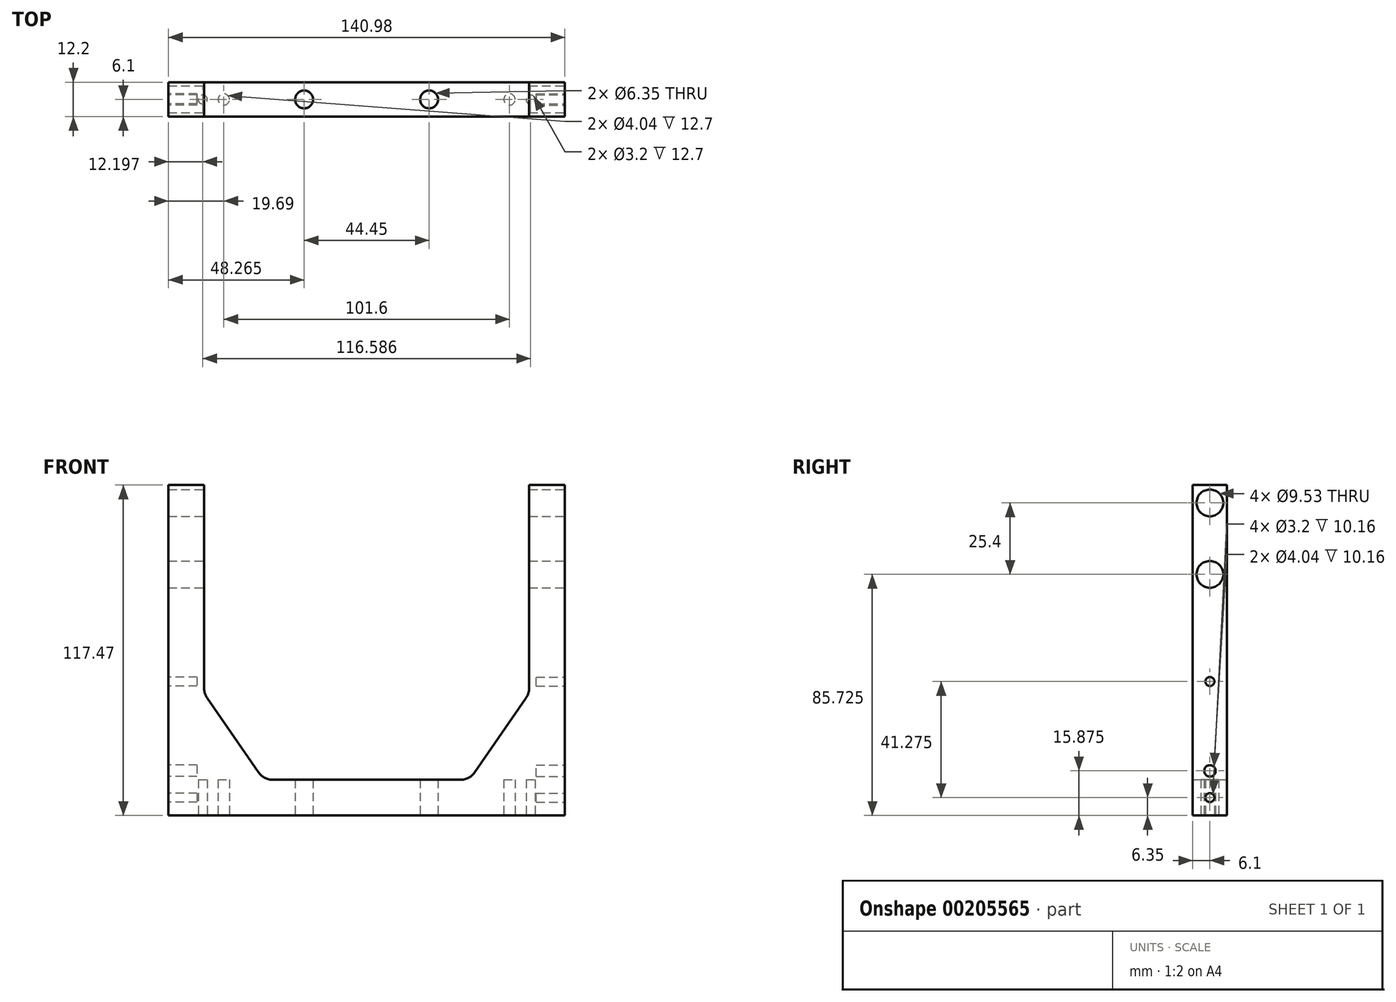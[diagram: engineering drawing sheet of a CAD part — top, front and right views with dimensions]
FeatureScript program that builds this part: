
annotation { "Feature Type Name" : "Feature", "Feature Type Description" : "" }
export const myFeature = defineFeature(function(context is Context, id is Id, definition is map)
    precondition{}
    {
        {
            var Q0;
            Q0=qCreatedBy(makeId("Front.planeOp"),FACE);
            var sketch = newSketch(context, id + "F0", { "sketchPlane" : qUnion([Q0])});
            skLineSegment(sketch, "E0", {"start": v(0, 0) * mm, "end": v(70.48, 0) * mm});
            skLineSegment(sketch, "E1", {"start": v(70.48, 0) * mm, "end": v(70.48, 117.48) * mm});
            skLineSegment(sketch, "E2", {"start": v(70.48, 117.48) * mm, "end": v(57.78, 117.48) * mm});
            skLineSegment(sketch, "E3", {"start": v(57.79, 117.48) * mm, "end": v(57.79, 45.31) * mm});
            skLineSegment(sketch, "E4", {"start": v(33.27, 12.7) * mm, "end": v(0, 12.7) * mm});
            skArc(sketch, "E5", {"start": v(56.66, 41.7) * mm, "mid": v(57.5, 43.42) * mm, "end": v(57.79, 45.31) * mm});
            skArc(sketch, "E6", {"start": v(33.27, 12.7) * mm, "mid": v(36.22, 13.43) * mm, "end": v(38.5, 15.44) * mm});
            skLineSegment(sketch, "E7", {"start": v(38.5, 15.44) * mm, "end": v(56.66, 41.7) * mm});
            skArc(sketch, "E8.MirrorCS", {"start": v(-33.27, 12.7) * mm, "mid": v(-36.22, 13.43) * mm, "end": v(-38.5, 15.44) * mm});
            skArc(sketch, "E9.MirrorCS", {"start": v(-56.66, 41.7) * mm, "mid": v(-57.5, 43.42) * mm, "end": v(-57.79, 45.31) * mm});
            skLineSegment(sketch, "E10.MirrorCS", {"start": v(0, 0) * mm, "end": v(-70.48, 0) * mm});
            skLineSegment(sketch, "E11.MirrorCS", {"start": v(-70.48, 0) * mm, "end": v(-70.48, 117.48) * mm});
            skLineSegment(sketch, "E12.MirrorCS", {"start": v(-57.79, 117.48) * mm, "end": v(-57.79, 45.31) * mm});
            skLineSegment(sketch, "E13.MirrorCS", {"start": v(-38.5, 15.44) * mm, "end": v(-56.66, 41.7) * mm});
            skLineSegment(sketch, "E14.MirrorCS", {"start": v(-33.27, 12.7) * mm, "end": v(0, 12.7) * mm});
            skLineSegment(sketch, "E15.MirrorCS", {"start": v(-70.48, 117.48) * mm, "end": v(-57.78, 117.48) * mm});
            skSolve(sketch);
        }
        {
            var Q0;
            Q0=qSketchRegion(id+"F0",true);
            extrude(context, id + "F1", {"entities" : qUnion([Q0]), "depth" : 12.2 * mm, "symmetric" : true});
        }
        {
            var Q0;
            Q0=makeQuery(id+"F1.opExtrude","SWEPT_FACE",FACE,{"disambiguationData":[OSD([sQuery(id+"F0.wireOp",EDGE,"E1")])]});
            var sketch = newSketch(context, id + "F2", { "sketchPlane" : qUnion([Q0])});
            skCircle(sketch, "E16", {"center": v(0, 111.13) * mm, "radius": 4.76 * mm});
            skCircle(sketch, "E17", {"center": v(0, 85.73) * mm, "radius": 4.76 * mm});
            skSolve(sketch);
        }
        {
            var Q0;
            Q0=qSketchRegion(id+"F2",true);
            extrude(context, id + "F3", {"entities" : qUnion([Q0]), "operationType" : NewBodyOperationType.REMOVE, "endBound" : BoundingType.THROUGH_ALL, "oppositeDirection" : true, "depth" : 25.4 * mm});
        }
        {
            var Q0;
            Q0=makeQuery(id+"F1.opExtrude","SWEPT_FACE",FACE,{"disambiguationData":[OSD([sQuery(id+"F0.wireOp",EDGE,"E0"),sQuery(id+"F0.wireOp",EDGE,"E10.MirrorCS")])]});
            var sketch = newSketch(context, id + "F4", { "sketchPlane" : qUnion([Q0])});
            skCircle(sketch, "E18", {"center": v(-22.23, 0) * mm, "radius": 3.18 * mm});
            skCircle(sketch, "E19", {"center": v(22.23, 0) * mm, "radius": 3.18 * mm});
            skSolve(sketch);
        }
        {
            var Q0;
            Q0=qSketchRegion(id+"F4",true);
            extrude(context, id + "F5", {"entities" : qUnion([Q0]), "operationType" : NewBodyOperationType.REMOVE, "endBound" : BoundingType.THROUGH_ALL, "oppositeDirection" : true, "depth" : 25.4 * mm});
        }
        {
            var Q0;
            Q0=makeQuery(id+"F1.opExtrude","SWEPT_FACE",FACE,{"disambiguationData":[OSD([sQuery(id+"F0.wireOp",EDGE,"E0"),sQuery(id+"F0.wireOp",EDGE,"E10.MirrorCS")])]});
            var sketch = newSketch(context, id + "F6", { "sketchPlane" : qUnion([Q0])});
            skCircle(sketch, "E20", {"center": v(-50.8, 0) * mm, "radius": 2.02 * mm});
            skCircle(sketch, "E21", {"center": v(-58.3, 0) * mm, "radius": 1.6 * mm});
            skCircle(sketch, "E22", {"center": v(50.8, 0) * mm, "radius": 2.02 * mm});
            skCircle(sketch, "E23", {"center": v(58.3, 0) * mm, "radius": 1.6 * mm});
            skSolve(sketch);
        }
        {
            var Q0;
            Q0=qSketchRegion(id+"F6",true);
            extrude(context, id + "F7", {"entities" : qUnion([Q0]), "operationType" : NewBodyOperationType.REMOVE, "oppositeDirection" : true, "depth" : 12.7 * mm});
        }
        {
            var Q0;
            Q0=makeQuery(id+"F1.opExtrude","SWEPT_FACE",FACE,{"disambiguationData":[OSD([sQuery(id+"F0.wireOp",EDGE,"E1")])]});
            var sketch = newSketch(context, id + "F8", { "sketchPlane" : qUnion([Q0])});
            skCircle(sketch, "E24", {"center": v(0, 6.35) * mm, "radius": 1.6 * mm});
            skCircle(sketch, "E25", {"center": v(0, 47.63) * mm, "radius": 1.6 * mm});
            skCircle(sketch, "E26", {"center": v(0, 15.88) * mm, "radius": 2.02 * mm});
            skSolve(sketch);
        }
        {
            var Q0;
            Q0=qSketchRegion(id+"F8",true);
            extrude(context, id + "F9", {"entities" : qUnion([Q0]), "operationType" : NewBodyOperationType.REMOVE, "oppositeDirection" : true, "depth" : 10.16 * mm});
        }
        {
            var Q0;
            Q0=makeQuery(id+"F1.opExtrude","SWEPT_FACE",FACE,{"disambiguationData":[OSD([sQuery(id+"F0.wireOp",EDGE,"E11.MirrorCS")])]});
            var sketch = newSketch(context, id + "F10", { "sketchPlane" : qUnion([Q0])});
            skCircle(sketch, "E27", {"center": v(0, 6.35) * mm, "radius": 1.6 * mm});
            skCircle(sketch, "E28", {"center": v(0, 15.88) * mm, "radius": 2.02 * mm});
            skCircle(sketch, "E29", {"center": v(0, 47.63) * mm, "radius": 1.6 * mm});
            skSolve(sketch);
        }
        {
            var Q0;
            Q0=qSketchRegion(id+"F10",true);
            extrude(context, id + "F11", {"entities" : qUnion([Q0]), "operationType" : NewBodyOperationType.REMOVE, "oppositeDirection" : true, "depth" : 10.16 * mm});
        }
    });
